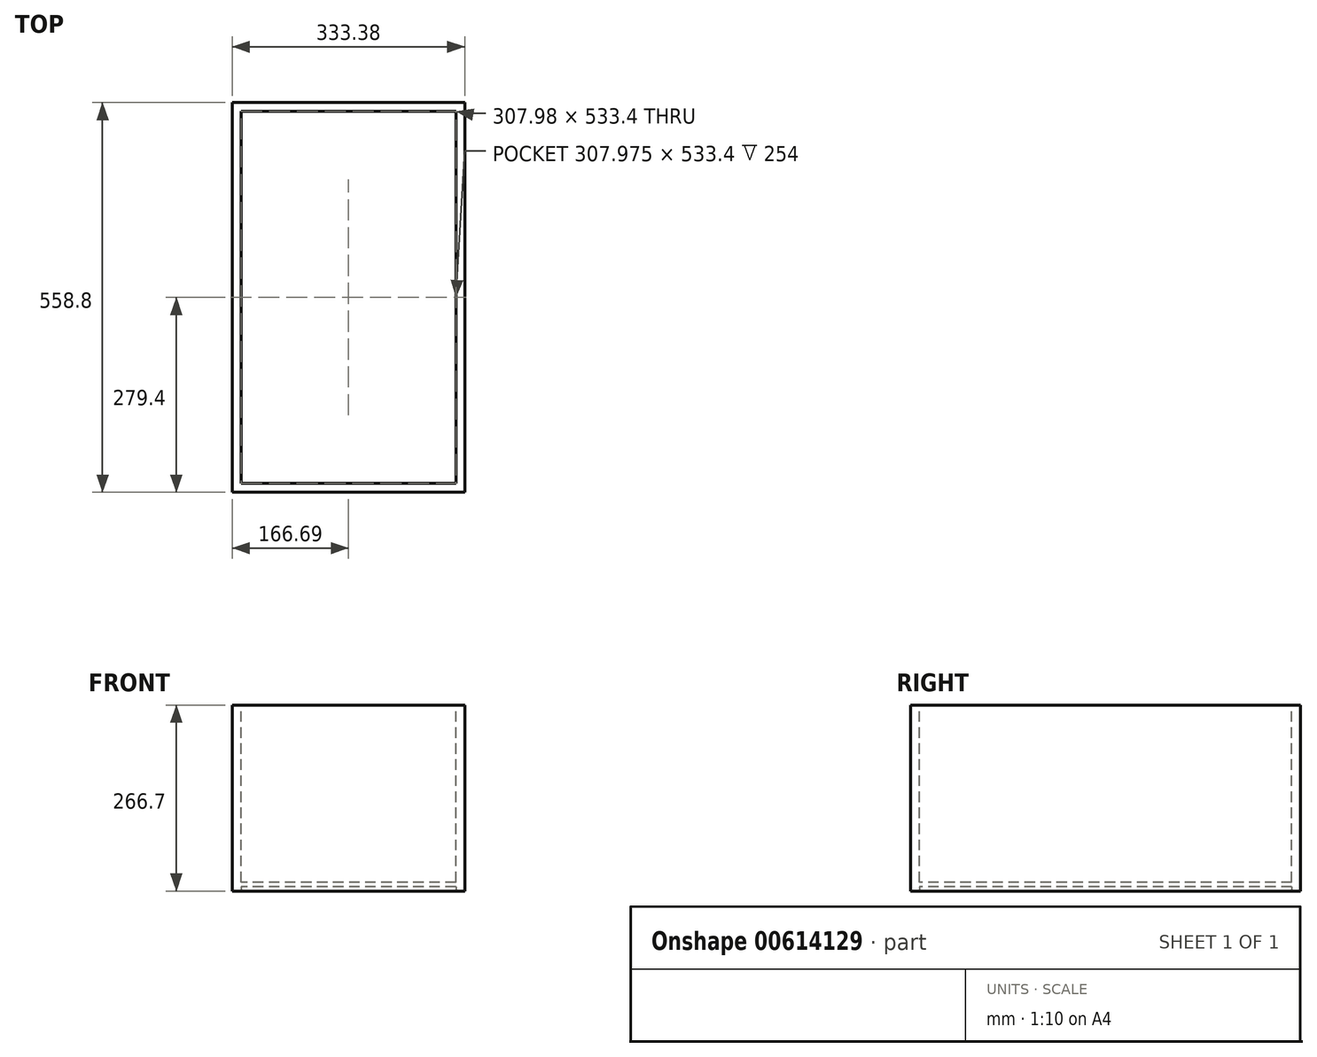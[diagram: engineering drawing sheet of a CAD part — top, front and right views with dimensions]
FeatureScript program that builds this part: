
annotation { "Feature Type Name" : "Feature", "Feature Type Description" : "" }
export const myFeature = defineFeature(function(context is Context, id is Id, definition is map)
    precondition{}
    {
        {
            var Q0;
            Q0=qCreatedBy(makeId("Top.planeOp"),FACE);
            var sketch = newSketch(context, id + "F0", { "sketchPlane" : qUnion([Q0])});
            skLineSegment(sketch, "E0.bottom", {"start": v(166.69, 279.4) * mm, "end": v(-166.69, 279.4) * mm});
            skLineSegment(sketch, "E0.top", {"start": v(166.69, -279.4) * mm, "end": v(-166.69, -279.4) * mm});
            skLineSegment(sketch, "E0.left", {"start": v(166.69, 279.4) * mm, "end": v(166.69, -279.4) * mm});
            skLineSegment(sketch, "E0.right", {"start": v(-166.69, 279.4) * mm, "end": v(-166.69, -279.4) * mm});
            skPoint(sketch, "E0.middle", {"position": v(0, 0) * mm});
            skSolve(sketch);
        }
        {
            var Q0;
            Q0=makeQuery(id+"F0.imprint","IMPRINT",FACE,{"disambiguationData":[TD([[makeQuery(id+"F0.imprint","IMPRINT",EDGE,{"derivedFrom":sQuery(id+"F0.wireOp",EDGE,"E0.bottom")}),1.0]])]});
            extrude(context, id + "F1", {"entities" : qUnion([Q0]), "depth" : 266.7 * mm, "offsetDistance" : 25.4 * mm});
        }
        {
            var Q0;
            Q0=makeQuery(id+"F1.opExtrude","CAP_FACE",FACE,{"disambiguationData":[OSD([sQuery(id+"F0.wireOp",EDGE,"E0.bottom"),sQuery(id+"F0.wireOp",EDGE,"E0.top"),sQuery(id+"F0.wireOp",EDGE,"E0.left"),sQuery(id+"F0.wireOp",EDGE,"E0.right")])],"isStart":false});
            var sketch = newSketch(context, id + "F2", { "sketchPlane" : qUnion([Q0])});
            skLineSegment(sketch, "E1.bottom", {"start": v(153.99, 266.7) * mm, "end": v(-153.99, 266.7) * mm});
            skLineSegment(sketch, "E1.top", {"start": v(153.99, -266.7) * mm, "end": v(-153.99, -266.7) * mm});
            skLineSegment(sketch, "E1.left", {"start": v(153.99, 266.7) * mm, "end": v(153.99, -266.7) * mm});
            skLineSegment(sketch, "E1.right", {"start": v(-153.99, 266.7) * mm, "end": v(-153.99, -266.7) * mm});
            skPoint(sketch, "E1.middle", {"position": v(0, 0) * mm});
            skSolve(sketch);
        }
        {
            var Q0;
            Q0=makeQuery(id+"F2.imprint","IMPRINT",FACE,{"disambiguationData":[TD([[makeQuery(id+"F2.imprint","IMPRINT",EDGE,{"derivedFrom":sQuery(id+"F2.wireOp",EDGE,"E1.bottom")}),1.0]])]});
            extrude(context, id + "F3", {"entities" : qUnion([Q0]), "operationType" : NewBodyOperationType.REMOVE, "oppositeDirection" : true, "depth" : 254 * mm, "offsetDistance" : 25.4 * mm});
        }
        {
            var Q0;
            Q0=makeQuery(id+"F1.opExtrude","CAP_FACE",FACE,{"disambiguationData":[OSD([sQuery(id+"F0.wireOp",EDGE,"E0.bottom"),sQuery(id+"F0.wireOp",EDGE,"E0.top"),sQuery(id+"F0.wireOp",EDGE,"E0.left"),sQuery(id+"F0.wireOp",EDGE,"E0.right")])],"isStart":true});
            var sketch = newSketch(context, id + "F4", { "sketchPlane" : qUnion([Q0])});
            skLineSegment(sketch, "E2.bottom", {"start": v(153.99, -266.7) * mm, "end": v(-153.99, -266.7) * mm});
            skLineSegment(sketch, "E2.top", {"start": v(153.99, 266.7) * mm, "end": v(-153.99, 266.7) * mm});
            skLineSegment(sketch, "E2.left", {"start": v(153.99, -266.7) * mm, "end": v(153.99, 266.7) * mm});
            skLineSegment(sketch, "E2.right", {"start": v(-153.99, -266.7) * mm, "end": v(-153.99, 266.7) * mm});
            skPoint(sketch, "E2.middle", {"position": v(0, 0) * mm});
            skSolve(sketch);
        }
        {
            var Q0;
            Q0=makeQuery(id+"F4.imprint","IMPRINT",FACE,{"disambiguationData":[TD([[makeQuery(id+"F4.imprint","IMPRINT",EDGE,{"derivedFrom":sQuery(id+"F4.wireOp",EDGE,"E2.bottom")}),-1.0]])]});
            extrude(context, id + "F5", {"entities" : qUnion([Q0]), "operationType" : NewBodyOperationType.REMOVE, "oppositeDirection" : true, "depth" : 6.35 * mm, "offsetDistance" : 25.4 * mm});
        }
    });
